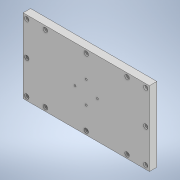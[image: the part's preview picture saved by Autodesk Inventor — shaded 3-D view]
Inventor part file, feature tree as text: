
AUTODESK INVENTOR PART (.ipt)
format: ipt  version: 2022.2 (Build 262287030, 287C)  size: 146,944 bytes
history: native  units: in
note: dims shown in document units (in); Inventor stores cm internally (conversion verified against a paired STEP export)
features: hole x2, sketch x2, extrude x1
ambient origin geometry x8: Origin, YZ Plane, XZ Plane, XY Plane, X Axis, Y Axis, Z Axis, Center Point
bodies: Solid1 (feature_tree)
feature tree (5):
  extrude  "Extrusion1"  Depth=3.937in
  hole  "Hole1"  [1 undecoded]
  hole  "Hole2"  [1 undecoded]
  sketch  "Sketch1"  dims[d0=6.6929in d1=3.937in]
  sketch  "Sketch3"  dims[d2=0.3937in d3=0.0in d4=0.1969in d5=0.1969in d8=3.1496in d13=0.9843in d14=0.1969in d16=0.1969in d17=0.0968in d18=0.2362in d19=0.2362in d20=0.0787in d21=90.0deg d22=0.5906in d23=0.0in d60=0.1969in d61=0.1969in d62=0.9843in d63=1.1811in d65=1.7717in d66=0.3937in d68=0.3937in d70=0.7874in d72=3.5433in d73=0.3937in d75=0.3937in d105=0.5906in d106=1.5748in d108=360.0deg d110=0.0984in d111=0.328in d112=0.1476in d113=0.0984in d114=90.0deg d115=0.1181in d116=0.0in]
note: 2 required parameter values undecoded (feature->parameter linkage not recoverable at this tier; creation-order binding heuristic only, values carry confidence <= 0.55)
